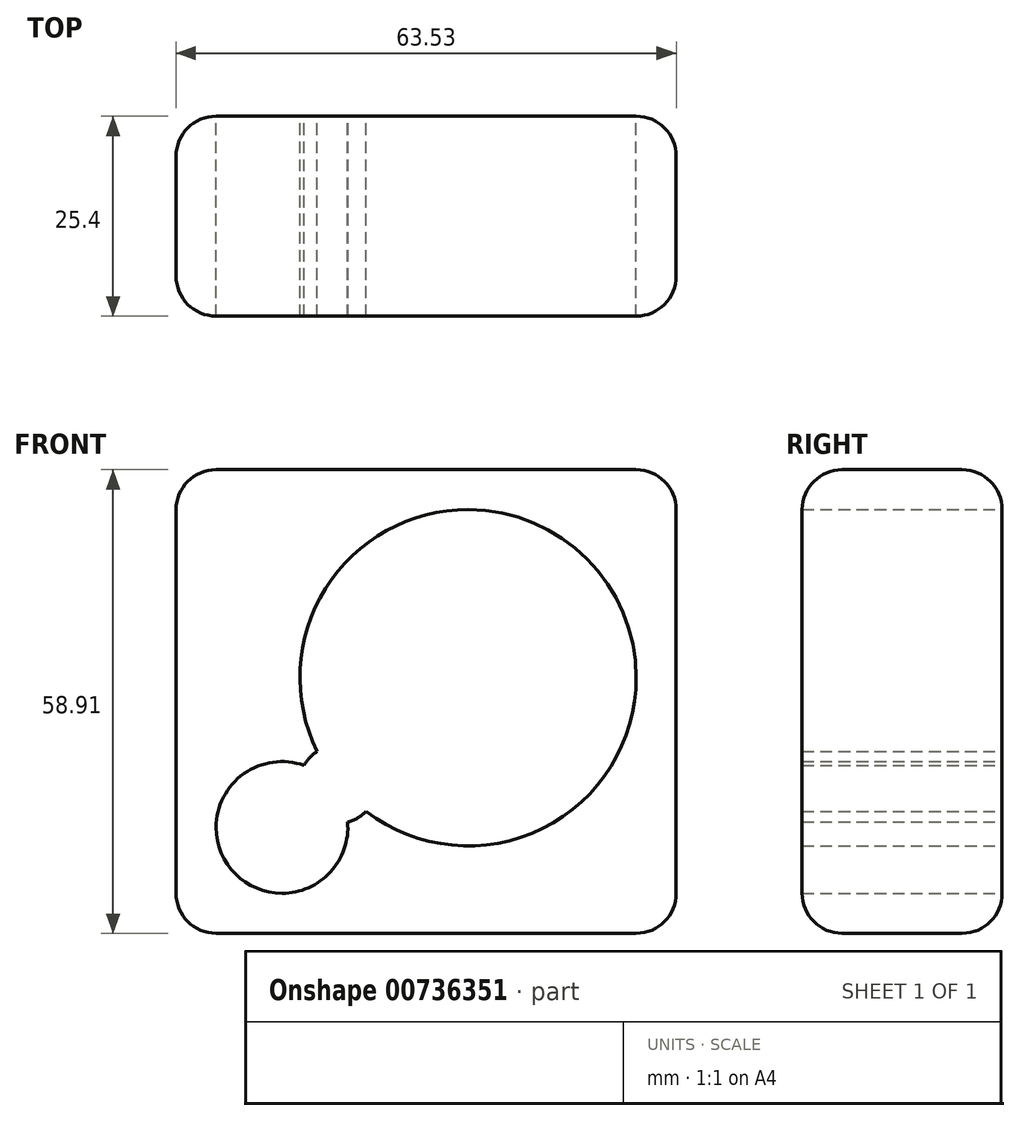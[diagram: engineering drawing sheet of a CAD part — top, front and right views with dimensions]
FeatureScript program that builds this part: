
annotation { "Feature Type Name" : "Feature", "Feature Type Description" : "" }
export const myFeature = defineFeature(function(context is Context, id is Id, definition is map)
    precondition{}
    {
        {
            var Q0;
            Q0=qCreatedBy(makeId("Front.planeOp"),FACE);
            var sketch = newSketch(context, id + "F0", { "sketchPlane" : qUnion([Q0])});
            skLineSegment(sketch, "E0.bottom", {"start": v(-24.63, 26.44) * mm, "end": v(38.9, 26.44) * mm});
            skLineSegment(sketch, "E0.top", {"start": v(-24.63, -32.47) * mm, "end": v(38.9, -32.47) * mm});
            skLineSegment(sketch, "E0.left", {"start": v(-24.63, 26.44) * mm, "end": v(-24.63, -32.47) * mm});
            skLineSegment(sketch, "E0.right", {"start": v(38.9, 26.44) * mm, "end": v(38.9, -32.47) * mm});
            skSolve(sketch);
        }
        {
            var Q0;
            Q0 = qSketchRegion(id + "F0", true);
            extrude(context, id + "F1", {"entities" : qUnion([Q0]), "depth" : 25.4 * mm, "offsetDistance" : 25.4 * mm});
        }
        {
            var Q0;
            Q0=makeQuery(id+"F1.opExtrude","CAP_EDGE",EDGE,{"disambiguationData":[OSD([sQuery(id+"F0.wireOp",EDGE,"E0.bottom")])],"isStart":false});
            var Q1;
            Q1=makeQuery(id+"F1.opExtrude","CAP_EDGE",EDGE,{"disambiguationData":[OSD([sQuery(id+"F0.wireOp",EDGE,"E0.left")])],"isStart":false});
            var Q2;
            Q2=makeQuery(id+"F1.opExtrude","CAP_EDGE",EDGE,{"disambiguationData":[OSD([sQuery(id+"F0.wireOp",EDGE,"E0.top")])],"isStart":false});
            var Q3;
            Q3=makeQuery(id+"F1.opExtrude","CAP_EDGE",EDGE,{"disambiguationData":[OSD([sQuery(id+"F0.wireOp",EDGE,"E0.right")])],"isStart":false});
            fillet(context, id + "F2", {"entities" : qUnion([Q0, Q1, Q2, Q3]), "radius" : 5.08 * mm, "tangentPropagation" : true, "allowEdgeOverflow" : false});
        }
        {
            var Q0;
            Q0=makeQuery(id+"F1.opExtrude","CAP_EDGE",EDGE,{"disambiguationData":[OSD([sQuery(id+"F0.wireOp",EDGE,"E0.bottom")])],"isStart":true});
            var Q1;
            Q1=makeQuery(id+"F1.opExtrude","CAP_EDGE",EDGE,{"disambiguationData":[OSD([sQuery(id+"F0.wireOp",EDGE,"E0.right")])],"isStart":true});
            var Q2;
            Q2=makeQuery(id+"F1.opExtrude","CAP_EDGE",EDGE,{"disambiguationData":[OSD([sQuery(id+"F0.wireOp",EDGE,"E0.left")])],"isStart":true});
            var Q3;
            Q3=makeQuery(id+"F1.opExtrude","CAP_EDGE",EDGE,{"disambiguationData":[OSD([sQuery(id+"F0.wireOp",EDGE,"E0.top")])],"isStart":true});
            fillet(context, id + "F3", {"entities" : qUnion([Q0, Q1, Q2, Q3]), "radius" : 5.08 * mm, "tangentPropagation" : true, "allowEdgeOverflow" : false});
        }
        {
            var Q0;
            Q0=makeQuery(id+"F1.opExtrude","SWEPT_EDGE",EDGE,{"disambiguationData":[OSD([sQuery(id+"F0.wireOp",EDGE,"E0.bottom"),sQuery(id+"F0.wireOp",EDGE,"E0.right")])]});
            var Q1;
            Q1=makeQuery(id+"F1.opExtrude","SWEPT_EDGE",EDGE,{"disambiguationData":[OSD([sQuery(id+"F0.wireOp",EDGE,"E0.top"),sQuery(id+"F0.wireOp",EDGE,"E0.right")])]});
            var Q2;
            Q2=makeQuery(id+"F1.opExtrude","SWEPT_EDGE",EDGE,{"disambiguationData":[OSD([sQuery(id+"F0.wireOp",EDGE,"E0.bottom"),sQuery(id+"F0.wireOp",EDGE,"E0.left")])]});
            var Q3;
            Q3=makeQuery(id+"F1.opExtrude","SWEPT_EDGE",EDGE,{"disambiguationData":[OSD([sQuery(id+"F0.wireOp",EDGE,"E0.top"),sQuery(id+"F0.wireOp",EDGE,"E0.left")])]});
            fillet(context, id + "F4", {"entities" : qUnion([Q0, Q1, Q2, Q3]), "radius" : 5.08 * mm, "tangentPropagation" : true, "allowEdgeOverflow" : false});
        }
        {
            var Q0;
            Q0=makeQuery(id+"F1.opExtrude","CAP_FACE",FACE,{"disambiguationData":[OSD([sQuery(id+"F0.wireOp",EDGE,"E0.bottom"),sQuery(id+"F0.wireOp",EDGE,"E0.top"),sQuery(id+"F0.wireOp",EDGE,"E0.left"),sQuery(id+"F0.wireOp",EDGE,"E0.right")])],"isStart":true});
            var sketch = newSketch(context, id + "F5", { "sketchPlane" : qUnion([Q0])});
            skCircle(sketch, "E1", {"center": v(-12.46, 0) * mm, "radius": 21.36 * mm});
            skCircle(sketch, "E2", {"center": v(11.18, -19.02) * mm, "radius": 8.37 * mm});
            skCircle(sketch, "E3", {"center": v(4.05, -13.54) * mm, "radius": 4.95 * mm});
            skSolve(sketch);
        }
        {
            var Q0;
            Q0 = qSketchRegion(id + "F5", true);
            extrude(context, id + "F6", {"entities" : qUnion([Q0]), "operationType" : NewBodyOperationType.REMOVE, "endBound" : BoundingType.THROUGH_ALL, "oppositeDirection" : true, "depth" : 25.4 * mm, "offsetDistance" : 25.4 * mm});
        }
    });
